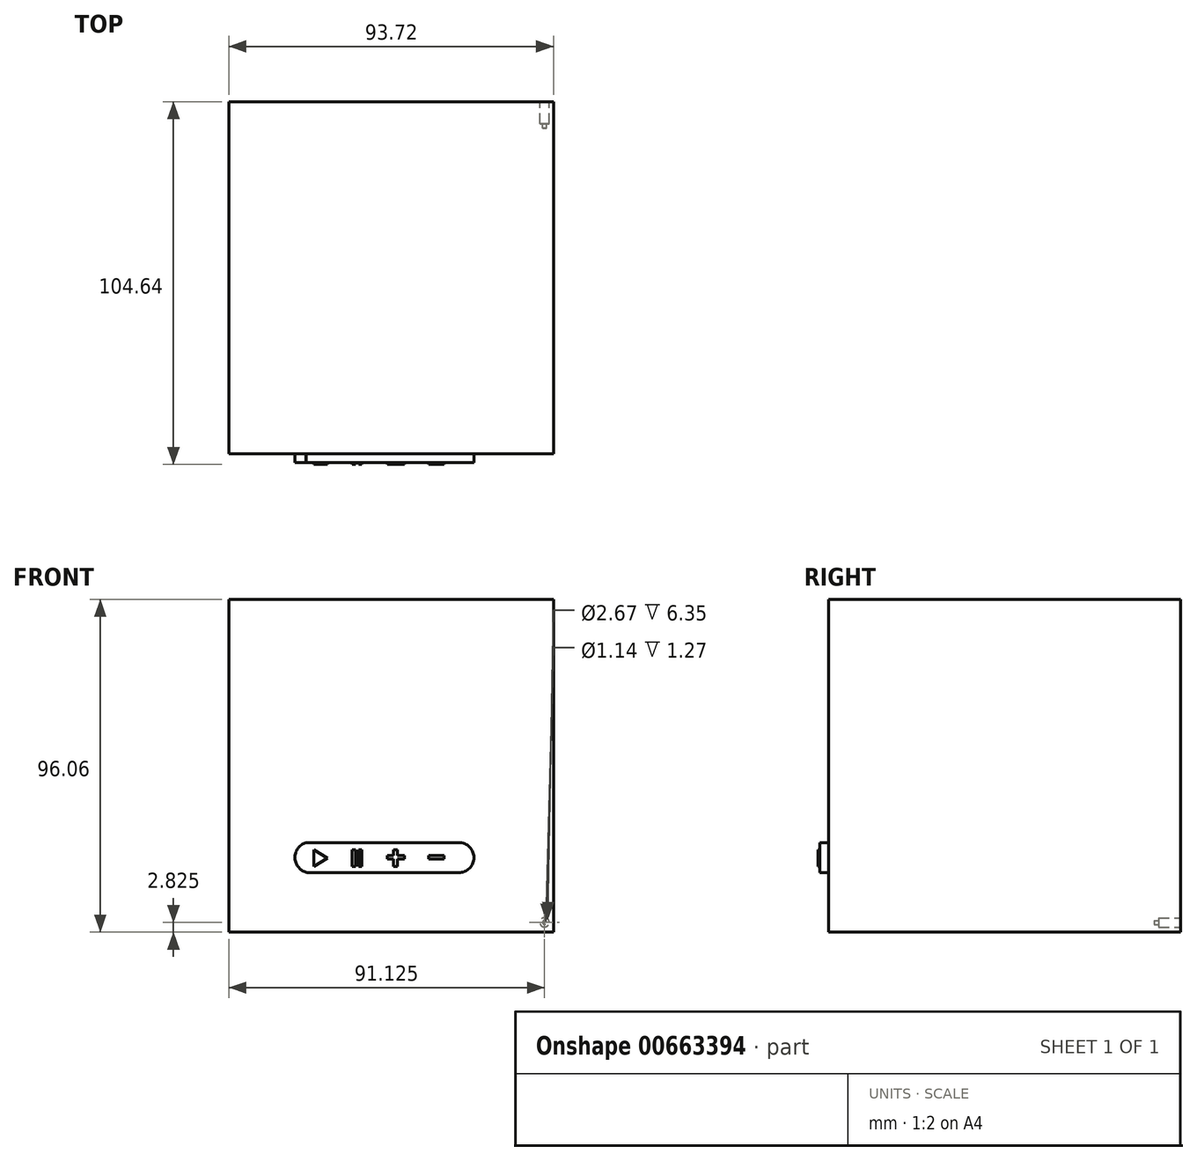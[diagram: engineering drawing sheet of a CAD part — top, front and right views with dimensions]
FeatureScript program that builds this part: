
annotation { "Feature Type Name" : "Feature", "Feature Type Description" : "" }
export const myFeature = defineFeature(function(context is Context, id is Id, definition is map)
    precondition{}
    {
        {
            var Q0;
            Q0=qCreatedBy(makeId("Front.planeOp"),FACE);
            var sketch = newSketch(context, id + "F0", { "sketchPlane" : qUnion([Q0])});
            skLineSegment(sketch, "E0.bottom", {"start": v(-47.5, 49.33) * mm, "end": v(46.2, 49.33) * mm});
            skLineSegment(sketch, "E0.top", {"start": v(-47.5, -46.73) * mm, "end": v(46.2, -46.73) * mm});
            skLineSegment(sketch, "E0.left", {"start": v(-47.5, 49.33) * mm, "end": v(-47.5, -46.73) * mm});
            skLineSegment(sketch, "E0.right", {"start": v(46.2, 49.33) * mm, "end": v(46.2, -46.73) * mm});
            skSolve(sketch);
        }
        {
            var Q0;
            Q0 = qSketchRegion(id + "F0", true);
            extrude(context, id + "F1", {"entities" : qUnion([Q0]), "depth" : 101.6 * mm, "offsetDistance" : 25.4 * mm});
        }
        {
            var Q0;
            Q0=makeQuery(id+"F1.opExtrude","CAP_FACE",FACE,{"disambiguationData":[OSD([sQuery(id+"F0.wireOp",EDGE,"E0.bottom"),sQuery(id+"F0.wireOp",EDGE,"E0.top"),sQuery(id+"F0.wireOp",EDGE,"E0.left"),sQuery(id+"F0.wireOp",EDGE,"E0.right")])],"isStart":false});
            var sketch = newSketch(context, id + "F2", { "sketchPlane" : qUnion([Q0])});
            skArc(sketch, "E1", {"start": v(-25.23, -20.85) * mm, "mid": v(-28.42, -25.36) * mm, "end": v(-24.83, -29.55) * mm});
            skLineSegment(sketch, "E2", {"start": v(-25.23, -20.85) * mm, "end": v(18.87, -20.85) * mm});
            skLineSegment(sketch, "E3", {"start": v(-24.83, -29.55) * mm, "end": v(18.87, -29.55) * mm});
            skArc(sketch, "E4", {"start": v(18.87, -29.55) * mm, "mid": v(23.22, -25.2) * mm, "end": v(18.87, -20.85) * mm});
            skLineSegment(sketch, "E5", {"start": v(-19.57, -20.85) * mm, "end": v(-19.57, -29.55) * mm});
            skLineSegment(sketch, "E6", {"start": v(-11.27, -29.55) * mm, "end": v(-11.27, -20.85) * mm});
            skLineSegment(sketch, "E7", {"start": v(-3.18, -20.85) * mm, "end": v(-3.18, -29.55) * mm});
            skLineSegment(sketch, "E8", {"start": v(5.11, -20.85) * mm, "end": v(5.11, -29.55) * mm});
            skLineSegment(sketch, "E9", {"start": v(13, -20.85) * mm, "end": v(13, -29.55) * mm});
            skSolve(sketch);
        }
        {
            var Q0;
            Q0 = qSketchRegion(id + "F2", true);
            extrude(context, id + "F3", {"entities" : qUnion([Q0]), "operationType" : NewBodyOperationType.ADD, "depth" : 2.54 * mm, "offsetDistance" : 25.4 * mm});
        }
        {
            var Q0;
            Q0=makeQuery(id+"F1.opExtrude","CAP_FACE",FACE,{"disambiguationData":[OSD([sQuery(id+"F0.wireOp",EDGE,"E0.bottom"),sQuery(id+"F0.wireOp",EDGE,"E0.top"),sQuery(id+"F0.wireOp",EDGE,"E0.left"),sQuery(id+"F0.wireOp",EDGE,"E0.right")])],"isStart":false});
            var sketch = newSketch(context, id + "F4", { "sketchPlane" : qUnion([Q0])});
            skLineSegment(sketch, "E10", {"start": v(-22.94, -22.94) * mm, "end": v(-22.94, -27.77) * mm});
            skLineSegment(sketch, "E11", {"start": v(-22.94, -22.94) * mm, "end": v(-19.02, -25.35) * mm});
            skPoint(sketch, "E11.endSnap0", {"position": v(-22.94, -25.35) * mm});
            skLineSegment(sketch, "E12", {"start": v(-22.94, -27.77) * mm, "end": v(-19.02, -25.35) * mm});
            skSolve(sketch);
        }
        {
            var Q0;
            Q0 = qSketchRegion(id + "F4", true);
            extrude(context, id + "F5", {"entities" : qUnion([Q0]), "operationType" : NewBodyOperationType.ADD, "depth" : 3 * mm, "offsetDistance" : 25.4 * mm});
        }
        {
            var Q0;
            Q0=makeQuery(id+"F3.opExtrude","CAP_FACE",FACE,{"disambiguationData":[OSD([sQuery(id+"F2.wireOp",EDGE,"E1"),sQuery(id+"F2.wireOp",EDGE,"E2"),sQuery(id+"F2.wireOp",EDGE,"E3"),sQuery(id+"F2.wireOp",EDGE,"E4")])],"isStart":false});
            var sketch = newSketch(context, id + "F6", { "sketchPlane" : qUnion([Q0])});
            skLineSegment(sketch, "E13", {"start": v(-11.9, -22.94) * mm, "end": v(-11.9, -27.77) * mm});
            skLineSegment(sketch, "E14", {"start": v(-11.9, -22.94) * mm, "end": v(-10.93, -22.94) * mm});
            skLineSegment(sketch, "E15", {"start": v(-10.93, -22.94) * mm, "end": v(-10.93, -27.77) * mm});
            skLineSegment(sketch, "E16", {"start": v(-10.93, -27.77) * mm, "end": v(-11.9, -27.77) * mm});
            skLineSegment(sketch, "E17", {"start": v(-10.01, -22.94) * mm, "end": v(-10.01, -27.77) * mm});
            skLineSegment(sketch, "E18", {"start": v(-10.01, -27.77) * mm, "end": v(-9.19, -27.77) * mm});
            skLineSegment(sketch, "E19", {"start": v(-9.19, -27.77) * mm, "end": v(-9.19, -22.94) * mm});
            skLineSegment(sketch, "E20", {"start": v(-9.19, -22.94) * mm, "end": v(-10.01, -22.94) * mm});
            skSolve(sketch);
        }
        {
            var Q0;
            Q0 = qSketchRegion(id + "F6", true);
            extrude(context, id + "F7", {"entities" : qUnion([Q0]), "operationType" : NewBodyOperationType.ADD, "depth" : 0.5 * mm, "offsetDistance" : 25.4 * mm});
        }
        {
            var Q0;
            Q0=makeQuery(id+"F3.opExtrude","CAP_FACE",FACE,{"disambiguationData":[OSD([sQuery(id+"F2.wireOp",EDGE,"E1"),sQuery(id+"F2.wireOp",EDGE,"E2"),sQuery(id+"F2.wireOp",EDGE,"E3"),sQuery(id+"F2.wireOp",EDGE,"E4")])],"isStart":false});
            var sketch = newSketch(context, id + "F8", { "sketchPlane" : qUnion([Q0])});
            skLineSegment(sketch, "E21.bottom", {"start": v(0, -27.77) * mm, "end": v(1.13, -27.77) * mm});
            skLineSegment(sketch, "E21.top", {"start": v(0, -22.94) * mm, "end": v(1.13, -22.94) * mm});
            skLineSegment(sketch, "E21.left", {"start": v(0, -27.77) * mm, "end": v(0, -22.94) * mm});
            skLineSegment(sketch, "E21.right", {"start": v(1.13, -27.77) * mm, "end": v(1.13, -22.94) * mm});
            skSolve(sketch);
        }
        {
            var Q0;
            Q0 = qSketchRegion(id + "F8", true);
            extrude(context, id + "F9", {"entities" : qUnion([Q0]), "operationType" : NewBodyOperationType.ADD, "depth" : 0.5 * mm, "offsetDistance" : 25.4 * mm});
        }
        {
            var Q0;
            Q0=makeQuery(id+"F3.opExtrude","CAP_FACE",FACE,{"disambiguationData":[OSD([sQuery(id+"F2.wireOp",EDGE,"E1"),sQuery(id+"F2.wireOp",EDGE,"E2"),sQuery(id+"F2.wireOp",EDGE,"E3"),sQuery(id+"F2.wireOp",EDGE,"E4")])],"isStart":false});
            var sketch = newSketch(context, id + "F10", { "sketchPlane" : qUnion([Q0])});
            skLineSegment(sketch, "E22.bottom", {"start": v(-1.7, -24.63) * mm, "end": v(3.15, -24.63) * mm});
            skLineSegment(sketch, "E22.top", {"start": v(-1.7, -25.66) * mm, "end": v(3.15, -25.66) * mm});
            skLineSegment(sketch, "E22.left", {"start": v(-1.7, -24.63) * mm, "end": v(-1.7, -25.66) * mm});
            skLineSegment(sketch, "E22.right", {"start": v(3.15, -24.63) * mm, "end": v(3.15, -25.66) * mm});
            skSolve(sketch);
        }
        {
            var Q0;
            Q0 = qSketchRegion(id + "F10", true);
            extrude(context, id + "F11", {"entities" : qUnion([Q0]), "operationType" : NewBodyOperationType.ADD, "depth" : 0.5 * mm, "offsetDistance" : 25.4 * mm});
        }
        {
            var Q0;
            Q0=makeQuery(id+"F3.opExtrude","CAP_FACE",FACE,{"disambiguationData":[OSD([sQuery(id+"F2.wireOp",EDGE,"E1"),sQuery(id+"F2.wireOp",EDGE,"E2"),sQuery(id+"F2.wireOp",EDGE,"E3"),sQuery(id+"F2.wireOp",EDGE,"E4")])],"isStart":false});
            var sketch = newSketch(context, id + "F12", { "sketchPlane" : qUnion([Q0])});
            skLineSegment(sketch, "E23.bottom", {"start": v(10.14, -24.63) * mm, "end": v(14.58, -24.63) * mm});
            skLineSegment(sketch, "E23.top", {"start": v(10.14, -25.66) * mm, "end": v(14.58, -25.66) * mm});
            skLineSegment(sketch, "E23.left", {"start": v(10.14, -24.63) * mm, "end": v(10.14, -25.66) * mm});
            skLineSegment(sketch, "E23.right", {"start": v(14.58, -24.63) * mm, "end": v(14.58, -25.66) * mm});
            skSolve(sketch);
        }
        {
            var Q0;
            Q0 = qSketchRegion(id + "F12", true);
            extrude(context, id + "F13", {"entities" : qUnion([Q0]), "operationType" : NewBodyOperationType.ADD, "depth" : 0.5 * mm, "offsetDistance" : 25.4 * mm});
        }
        {
            var Q0;
            Q0=makeQuery(id+"F1.opExtrude","CAP_FACE",FACE,{"disambiguationData":[OSD([sQuery(id+"F0.wireOp",EDGE,"E0.bottom"),sQuery(id+"F0.wireOp",EDGE,"E0.top"),sQuery(id+"F0.wireOp",EDGE,"E0.left"),sQuery(id+"F0.wireOp",EDGE,"E0.right")])],"isStart":true});
            var sketch = newSketch(context, id + "F14", { "sketchPlane" : qUnion([Q0])});
            skCircle(sketch, "E24", {"center": v(-43.61, -43.9) * mm, "radius": 1.33 * mm});
            skSolve(sketch);
        }
        {
            var Q0;
            Q0 = qSketchRegion(id + "F14", true);
            extrude(context, id + "F15", {"entities" : qUnion([Q0]), "operationType" : NewBodyOperationType.REMOVE, "oppositeDirection" : true, "depth" : 6.35 * mm, "offsetDistance" : 25.4 * mm});
        }
        {
            var Q0;
            Q0=makeQuery(id+"F1.opExtrude","CAP_FACE",FACE,{"disambiguationData":[OSD([sQuery(id+"F0.wireOp",EDGE,"E0.bottom"),sQuery(id+"F0.wireOp",EDGE,"E0.top"),sQuery(id+"F0.wireOp",EDGE,"E0.left"),sQuery(id+"F0.wireOp",EDGE,"E0.right")])],"isStart":true});
            var sketch = newSketch(context, id + "F16", { "sketchPlane" : qUnion([Q0])});
            skCircle(sketch, "E25", {"center": v(-43.61, -43.9) * mm, "radius": 0.57 * mm});
            skSolve(sketch);
        }
        {
            var Q0;
            Q0 = qSketchRegion(id + "F16", true);
            extrude(context, id + "F17", {"entities" : qUnion([Q0]), "operationType" : NewBodyOperationType.REMOVE, "oppositeDirection" : true, "depth" : 7.62 * mm, "offsetDistance" : 25.4 * mm});
        }
    });
